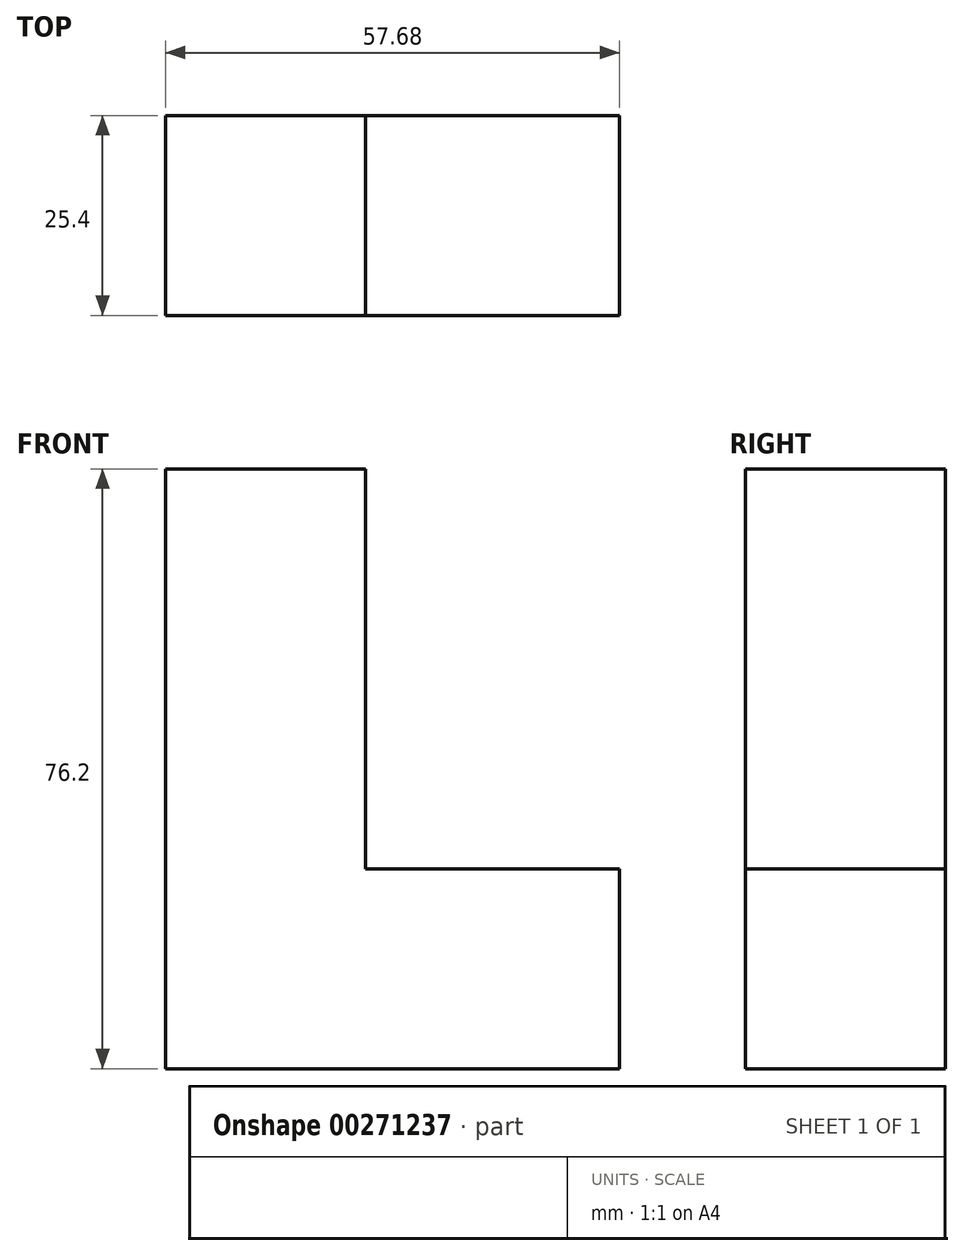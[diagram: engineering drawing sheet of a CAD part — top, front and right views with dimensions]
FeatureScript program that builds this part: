
annotation { "Feature Type Name" : "Feature", "Feature Type Description" : "" }
export const myFeature = defineFeature(function(context is Context, id is Id, definition is map)
    precondition{}
    {
        {
            var Q0;
            Q0=qCreatedBy(makeId("Front.planeOp"),FACE);
            var sketch = newSketch(context, id + "F0", { "sketchPlane" : qUnion([Q0])});
            skLineSegment(sketch, "E0", {"start": v(-75.84, 76.2) * mm, "end": v(-75.84, 0) * mm});
            skLineSegment(sketch, "E1", {"start": v(-75.84, 0) * mm, "end": v(-75.84, 76.2) * mm});
            skLineSegment(sketch, "E2", {"start": v(-75.84, 76.2) * mm, "end": v(-50.44, 76.2) * mm});
            skLineSegment(sketch, "E3", {"start": v(-50.44, 76.2) * mm, "end": v(-50.44, 25.4) * mm});
            skLineSegment(sketch, "E4", {"start": v(-50.44, 25.4) * mm, "end": v(-18.16, 25.4) * mm});
            skLineSegment(sketch, "E5", {"start": v(-18.16, 25.4) * mm, "end": v(-18.16, 0) * mm});
            skLineSegment(sketch, "E6", {"start": v(-18.16, 0) * mm, "end": v(-75.84, 0) * mm});
            skSolve(sketch);
        }
        {
            var Q0;
            Q0 = qSketchRegion(id + "F0", true);
            extrude(context, id + "F1", {"entities" : qUnion([Q0]), "depth" : 25.4 * mm});
        }
    });
